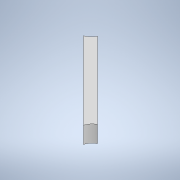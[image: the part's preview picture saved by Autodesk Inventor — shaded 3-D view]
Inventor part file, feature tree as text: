
AUTODESK INVENTOR PART (.ipt)
format: ipt  version: 2022 (Build 260153000, 153)  size: 282,112 bytes
history: native  units: mm
features: extrude x1, sketch x1
ambient origin geometry x8: Origin, YZ Plane, XZ Plane, XY Plane, X Axis, Y Axis, Z Axis, Center Point
bodies: Body1 (feature_tree)
feature tree (2):
  extrude  "Extrusion5"  Depth=5.0mm
  sketch  "Sketch1"  dims[d31=34.456mm d50=368.759386mm d57=16.0mm d69=8.0mm d70=23.0mm d71=8.0mm d73=16.0mm d80=19.0mm d81=16.0mm d82=1.0mm d83=1.0mm d84=1.0mm d85=1.0mm d86=1.0mm d87=0.8mm d88=1.0mm d90=19.0mm d94=5.0mm d95=5.0mm d105=5.0mm d106=5.0mm d108=2.0mm d109=19.0mm d114=5.0mm d115=5.0mm d116=24.0mm d117=2.5mm d118=2.5mm d123=2.5mm d124=2.5mm d125=10.0mm d126=24.0mm d127=24.0mm d128=27.0mm d135=0.5mm d136=45.0deg d139=7.0mm d165=45.0deg d169=27.0mm d175=90.0deg d181=45.0deg d185=7.0mm d186=45.0deg d190=7.0mm d191=45.0deg d197=90.0deg d203=90.0deg d206=7.0mm d207=5.0mm d208=0.0mm]
